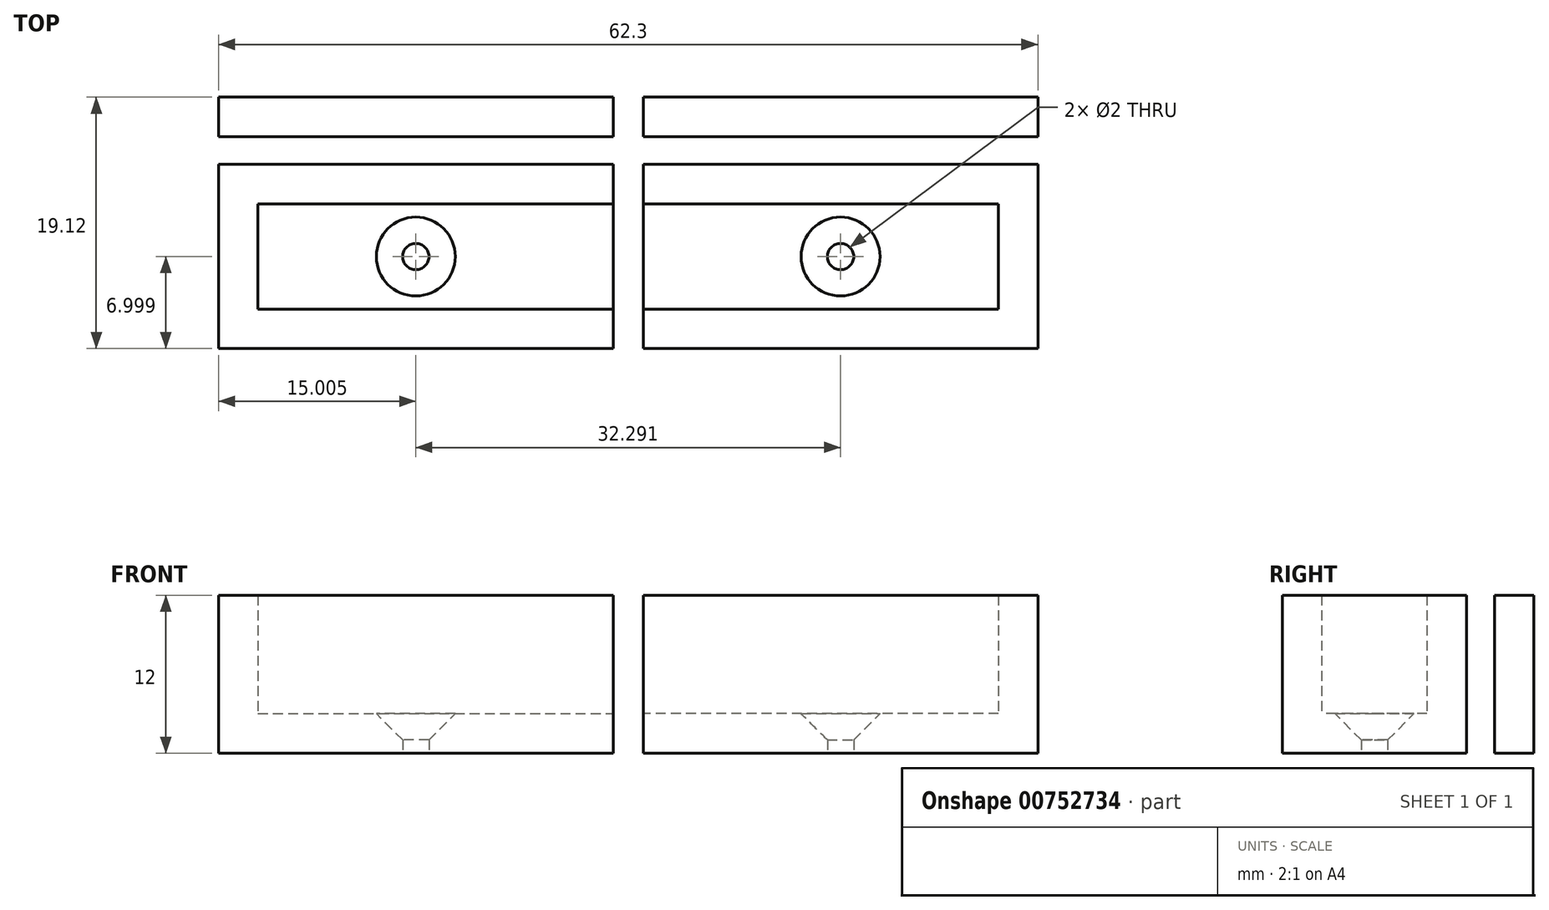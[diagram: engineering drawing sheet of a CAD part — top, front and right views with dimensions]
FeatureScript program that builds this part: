
annotation { "Feature Type Name" : "Feature", "Feature Type Description" : "" }
export const myFeature = defineFeature(function(context is Context, id is Id, definition is map)
    precondition{}
    {
        {
            var Q0;
            Q0=qCreatedBy(makeId("Top.planeOp"),FACE);
            var sketch = newSketch(context, id + "F0", { "sketchPlane" : qUnion([Q0])});
            skLineSegment(sketch, "E0.bottom", {"start": v(-42.05, -6.81) * mm, "end": v(-12.05, -6.81) * mm});
            skLineSegment(sketch, "E0.top", {"start": v(-42.05, -20.81) * mm, "end": v(-12.05, -20.81) * mm});
            skLineSegment(sketch, "E0.left", {"start": v(-42.05, -6.81) * mm, "end": v(-42.05, -20.81) * mm});
            skLineSegment(sketch, "E0.right", {"start": v(-12.05, -6.81) * mm, "end": v(-12.05, -20.81) * mm});
            skLineSegment(sketch, "E1.top", {"start": v(-42.05, -9.81) * mm, "end": v(-12.05, -9.81) * mm});
            skLineSegment(sketch, "E1.left", {"start": v(-42.05, -6.81) * mm, "end": v(-42.05, -9.81) * mm});
            skLineSegment(sketch, "E1.right", {"start": v(-12.05, -6.81) * mm, "end": v(-12.05, -9.81) * mm});
            skLineSegment(sketch, "E2.top", {"start": v(-42.05, -17.81) * mm, "end": v(-12.05, -17.81) * mm});
            skLineSegment(sketch, "E2.left", {"start": v(-42.05, -20.81) * mm, "end": v(-42.05, -17.81) * mm});
            skLineSegment(sketch, "E2.right", {"start": v(-12.05, -20.81) * mm, "end": v(-12.05, -17.81) * mm});
            skCircle(sketch, "E3", {"center": v(-27.05, -13.81) * mm, "radius": 1 * mm});
            skPoint(sketch, "E3.centerSnap0", {"position": v(-42.05, -13.81) * mm});
            skPoint(sketch, "E3.centerSnap1", {"position": v(-27.05, -6.81) * mm});
            skSolve(sketch);
        }
        {
            var Q0;
            {var subQ0=sQuery(id+"F0.wireOp",EDGE,"E0.bottom");Q0=makeQuery(id+"F0.imprint","IMPRINT",FACE,{"disambiguationData":[TD([[makeQuery(id+"F0.imprint","IMPRINT",EDGE,{"derivedFrom":subQ0}),-1.0]])]});}
            var Q1;
            {var subQ0=sQuery(id+"F0.wireOp",EDGE,"E0.top");Q1=makeQuery(id+"F0.imprint","IMPRINT",FACE,{"disambiguationData":[TD([[makeQuery(id+"F0.imprint","IMPRINT",EDGE,{"derivedFrom":subQ0}),1.0]])]});}
            extrude(context, id + "F1", {"entities" : qUnion([Q0, Q1]), "depth" : 12 * mm, "offsetDistance" : 25 * mm});
        }
        {
            var Q0;
            {var subQ1=sQuery(id+"F0.wireOp",EDGE,"E1.top");Q0=makeQuery(id+"F0.imprint","IMPRINT",FACE,{"disambiguationData":[TD([[makeQuery(id+"F0.imprint","IMPRINT",EDGE,{"derivedFrom":subQ1}),-1.0]])]});}
            extrude(context, id + "F2", {"entities" : qUnion([Q0]), "depth" : 3 * mm, "offsetDistance" : 25 * mm});
        }
        {
            var Q0;
            Q0=makeQuery(id+"F2.opExtrude","CAP_EDGE",EDGE,{"disambiguationData":[OSD([sQuery(id+"F0.wireOp",EDGE,"E3")])],"isStart":false});
            chamfer(context, id + "F3", {"entities" : qUnion([Q0]), "width" : 2 * mm, "tangentPropagation" : true});
        }
        {
            var Q0;
            Q0=makeQuery(id+"F1.opExtrude","SWEPT_BODY",BODY,{"disambiguationData":[OSD([sQuery(id+"F0.wireOp",EDGE,"E0.bottom"),sQuery(id+"F0.wireOp",EDGE,"E0.left"),sQuery(id+"F0.wireOp",EDGE,"E0.right"),sQuery(id+"F0.wireOp",EDGE,"E1.top")])]});
            var Q1;
            Q1=qCreatedBy(makeId("Front.planeOp"),FACE);
            mirror(context, id + "F4", {"entities" : qUnion([Q0]), "mirrorPlane" : qUnion([Q1])});
        }
        {
            var Q0;
            Q0=makeQuery(id+"F2.opExtrude","CAP_FACE",FACE,{"disambiguationData":[OSD([sQuery(id+"F0.wireOp",EDGE,"E0.left"),sQuery(id+"F0.wireOp",EDGE,"E0.right"),sQuery(id+"F0.wireOp",EDGE,"E1.top"),sQuery(id+"F0.wireOp",EDGE,"E2.top"),sQuery(id+"F0.wireOp",EDGE,"E3")])],"isStart":false});
            var sketch = newSketch(context, id + "F5", { "sketchPlane" : qUnion([Q0])});
            skLineSegment(sketch, "E4.bottom", {"start": v(-42.05, -17.81) * mm, "end": v(-39.05, -17.81) * mm});
            skLineSegment(sketch, "E4.top", {"start": v(-42.05, -9.81) * mm, "end": v(-39.05, -9.81) * mm});
            skLineSegment(sketch, "E4.left", {"start": v(-42.05, -17.81) * mm, "end": v(-42.05, -9.81) * mm});
            skLineSegment(sketch, "E4.right", {"start": v(-39.05, -17.81) * mm, "end": v(-39.05, -9.81) * mm});
            skSolve(sketch);
        }
        {
            var Q0;
            Q0=makeQuery(id+"F5.imprint","IMPRINT",FACE,{"disambiguationData":[TD([[makeQuery(id+"F5.imprint","IMPRINT",EDGE,{"derivedFrom":sQuery(id+"F5.wireOp",EDGE,"E4.bottom")}),1.0]])]});
            extrude(context, id + "F6", {"entities" : qUnion([Q0]), "operationType" : NewBodyOperationType.ADD, "depth" : 9 * mm, "offsetDistance" : 25 * mm});
        }
        {
            var Q0;
            Q0=makeQuery(id+"F1.opExtrude","SWEPT_BODY",BODY,{"disambiguationData":[OSD([sQuery(id+"F0.wireOp",EDGE,"E0.bottom"),sQuery(id+"F0.wireOp",EDGE,"E0.left"),sQuery(id+"F0.wireOp",EDGE,"E0.right"),sQuery(id+"F0.wireOp",EDGE,"E1.top")])]});
            var Q1;
            Q1=makeQuery(id+"F4.opPattern","COPY",BODY,{"derivedFrom":makeQuery(id+"F1.opExtrude","SWEPT_BODY",BODY,{"disambiguationData":[OSD([sQuery(id+"F0.wireOp",EDGE,"E0.bottom"),sQuery(id+"F0.wireOp",EDGE,"E0.left"),sQuery(id+"F0.wireOp",EDGE,"E0.right"),sQuery(id+"F0.wireOp",EDGE,"E1.top")])]}),"instanceName":"1"});
            var Q2;
            Q2=qCreatedBy(makeId("Right.planeOp"),FACE);
            mirror(context, id + "F7", {"entities" : qUnion([Q0, Q1]), "mirrorPlane" : qUnion([Q2])});
        }
        {
            var Q0;
            Q0=makeQuery(id+"F7.opPattern","COPY",BODY,{"derivedFrom":makeQuery(id+"F1.opExtrude","SWEPT_BODY",BODY,{"disambiguationData":[OSD([sQuery(id+"F0.wireOp",EDGE,"E0.bottom"),sQuery(id+"F0.wireOp",EDGE,"E0.left"),sQuery(id+"F0.wireOp",EDGE,"E0.right"),sQuery(id+"F0.wireOp",EDGE,"E1.top")])]}),"instanceName":"1"});
            transform(context, id + "F8", {"entities" : qUnion([Q0]), "transformType" : TransformType.TRANSLATION_3D, "dx" : -21.8 * mm, "dy" : 0 * mm, "dz" : 0 * mm, "makeCopy" : false});
        }
        {
            var Q0;
            Q0=makeQuery(id+"F7.opPattern","COPY",BODY,{"derivedFrom":makeQuery(id+"F4.opPattern","COPY",BODY,{"derivedFrom":makeQuery(id+"F1.opExtrude","SWEPT_BODY",BODY,{"disambiguationData":[OSD([sQuery(id+"F0.wireOp",EDGE,"E0.bottom"),sQuery(id+"F0.wireOp",EDGE,"E0.left"),sQuery(id+"F0.wireOp",EDGE,"E0.right"),sQuery(id+"F0.wireOp",EDGE,"E1.top")])]}),"instanceName":"1"}),"instanceName":"1"});
            transform(context, id + "F9", {"entities" : qUnion([Q0]), "transformType" : TransformType.TRANSLATION_3D, "dx" : -21.8 * mm, "dy" : 0 * mm, "dz" : 0 * mm, "makeCopy" : false});
        }
        {
            var Q0;
            Q0=makeQuery(id+"F1.opExtrude","SWEPT_BODY",BODY,{"disambiguationData":[OSD([sQuery(id+"F0.wireOp",EDGE,"E0.bottom"),sQuery(id+"F0.wireOp",EDGE,"E0.left"),sQuery(id+"F0.wireOp",EDGE,"E0.right"),sQuery(id+"F0.wireOp",EDGE,"E1.top")])]});
            var Q1;
            Q1=makeQuery(id+"F7.opPattern","COPY",BODY,{"derivedFrom":makeQuery(id+"F1.opExtrude","SWEPT_BODY",BODY,{"disambiguationData":[OSD([sQuery(id+"F0.wireOp",EDGE,"E0.bottom"),sQuery(id+"F0.wireOp",EDGE,"E0.left"),sQuery(id+"F0.wireOp",EDGE,"E0.right"),sQuery(id+"F0.wireOp",EDGE,"E1.top")])]}),"instanceName":"1"});
            transform(context, id + "F10", {"entities" : qUnion([Q0, Q1]), "transformType" : TransformType.TRANSLATION_3D, "dx" : 0 * mm, "dy" : 11.5 * mm, "dz" : 0 * mm, "makeCopy" : false});
        }
    });
